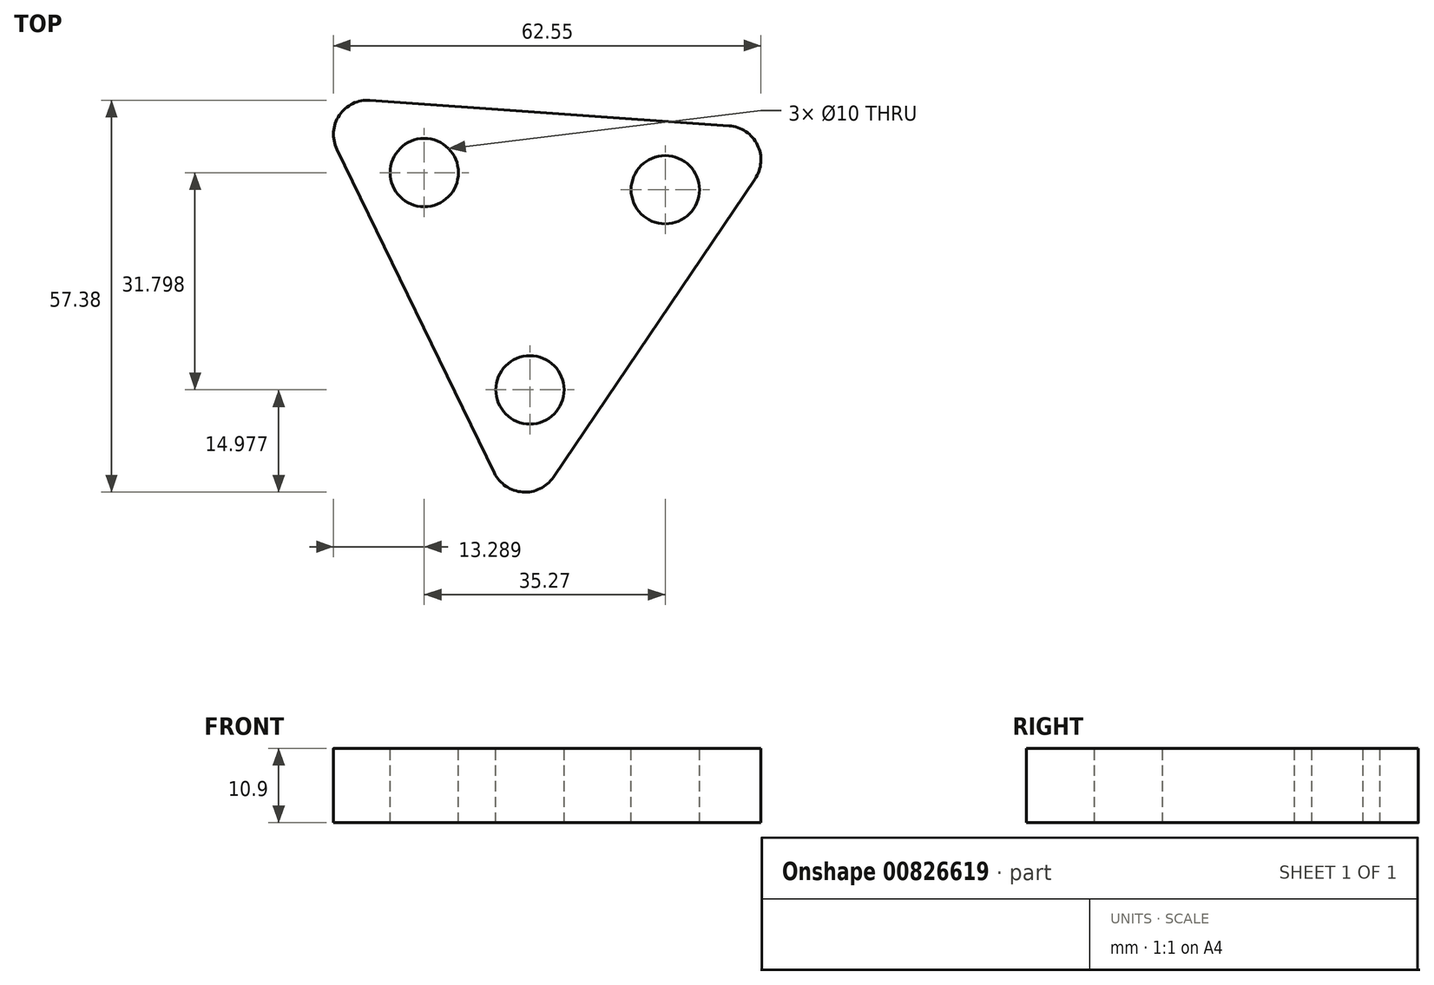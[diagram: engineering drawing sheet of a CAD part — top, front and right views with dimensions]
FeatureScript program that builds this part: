
annotation { "Feature Type Name" : "Feature", "Feature Type Description" : "" }
export const myFeature = defineFeature(function(context is Context, id is Id, definition is map)
    precondition{}
    {
        {
            var Q0;
            Q0=qCreatedBy(makeId("Top.planeOp"),FACE);
            var sketch = newSketch(context, id + "F0", { "sketchPlane" : qUnion([Q0])});
            skCircle(sketch, "E0.cCircle", {"center": v(0, 0) * mm, "radius": 20.2 * mm, "construction": true});
            skLineSegment(sketch, "E0.0", {"start": v(36.34, 17.67) * mm, "end": v(-2.87, -40.31) * mm});
            skLineSegment(sketch, "E0.1", {"start": v(-2.87, -40.31) * mm, "end": v(-33.48, 22.64) * mm});
            skLineSegment(sketch, "E0.2", {"start": v(-33.48, 22.64) * mm, "end": v(36.34, 17.67) * mm});
            skPoint(sketch, "E0.0.midPoint", {"position": v(16.74, -11.32) * mm});
            skSolve(sketch);
        }
        {
            var Q0;
            Q0=makeQuery(id+"F0.imprint","IMPRINT",FACE,{"disambiguationData":[TD([[makeQuery(id+"F0.imprint","IMPRINT",EDGE,{"derivedFrom":sQuery(id+"F0.wireOp",EDGE,"E0.0")}),-1.0]])]});
            extrude(context, id + "F1", {"entities" : qUnion([Q0]), "depth" : 10.9 * mm, "offsetDistance" : 25 * mm});
        }
        {
            var Q0;
            Q0=makeQuery(id+"F1.opExtrude","SWEPT_EDGE",EDGE,{"disambiguationData":[OSD([sQuery(id+"F0.wireOp",EDGE,"E0.0"),sQuery(id+"F0.wireOp",EDGE,"E0.2")])]});
            var Q1;
            Q1=makeQuery(id+"F1.opExtrude","SWEPT_EDGE",EDGE,{"disambiguationData":[OSD([sQuery(id+"F0.wireOp",EDGE,"E0.0"),sQuery(id+"F0.wireOp",EDGE,"E0.1")])]});
            var Q2;
            Q2=makeQuery(id+"F1.opExtrude","SWEPT_EDGE",EDGE,{"disambiguationData":[OSD([sQuery(id+"F0.wireOp",EDGE,"E0.1"),sQuery(id+"F0.wireOp",EDGE,"E0.2")])]});
            fillet(context, id + "F2", {"entities" : qUnion([Q0, Q1, Q2]), "radius" : 5 * mm, "tangentPropagation" : true, "allowEdgeOverflow" : false});
        }
        {
            var Q0;
            Q0=makeQuery(id+"F1.opExtrude","CAP_FACE",FACE,{"disambiguationData":[OSD([sQuery(id+"F0.wireOp",EDGE,"E0.0"),sQuery(id+"F0.wireOp",EDGE,"E0.1"),sQuery(id+"F0.wireOp",EDGE,"E0.2")])],"isStart":false});
            var sketch = newSketch(context, id + "F3", { "sketchPlane" : qUnion([Q0])});
            skCircle(sketch, "E1", {"center": v(-16.91, 11.44) * mm, "radius": 5 * mm});
            skCircle(sketch, "E2", {"center": v(18.36, 8.93) * mm, "radius": 5 * mm});
            skCircle(sketch, "E3", {"center": v(-1.45, -20.36) * mm, "radius": 5 * mm});
            skSolve(sketch);
        }
        {
            var Q0;
            Q0=makeQuery(id+"F3.imprint","IMPRINT",FACE,{"disambiguationData":[TD([[makeQuery(id+"F3.imprint","IMPRINT",EDGE,{"derivedFrom":sQuery(id+"F3.wireOp",EDGE,"E3")}),1.0]])]});
            var Q1;
            Q1=makeQuery(id+"F3.imprint","IMPRINT",FACE,{"disambiguationData":[TD([[makeQuery(id+"F3.imprint","IMPRINT",EDGE,{"derivedFrom":sQuery(id+"F3.wireOp",EDGE,"E2")}),1.0]])]});
            var Q2;
            Q2=makeQuery(id+"F3.imprint","IMPRINT",FACE,{"disambiguationData":[TD([[makeQuery(id+"F3.imprint","IMPRINT",EDGE,{"derivedFrom":sQuery(id+"F3.wireOp",EDGE,"E1")}),1.0]])]});
            extrude(context, id + "F4", {"entities" : qUnion([Q0, Q1, Q2]), "operationType" : NewBodyOperationType.REMOVE, "oppositeDirection" : true, "depth" : 25 * mm, "offsetDistance" : 25 * mm});
        }
    });
